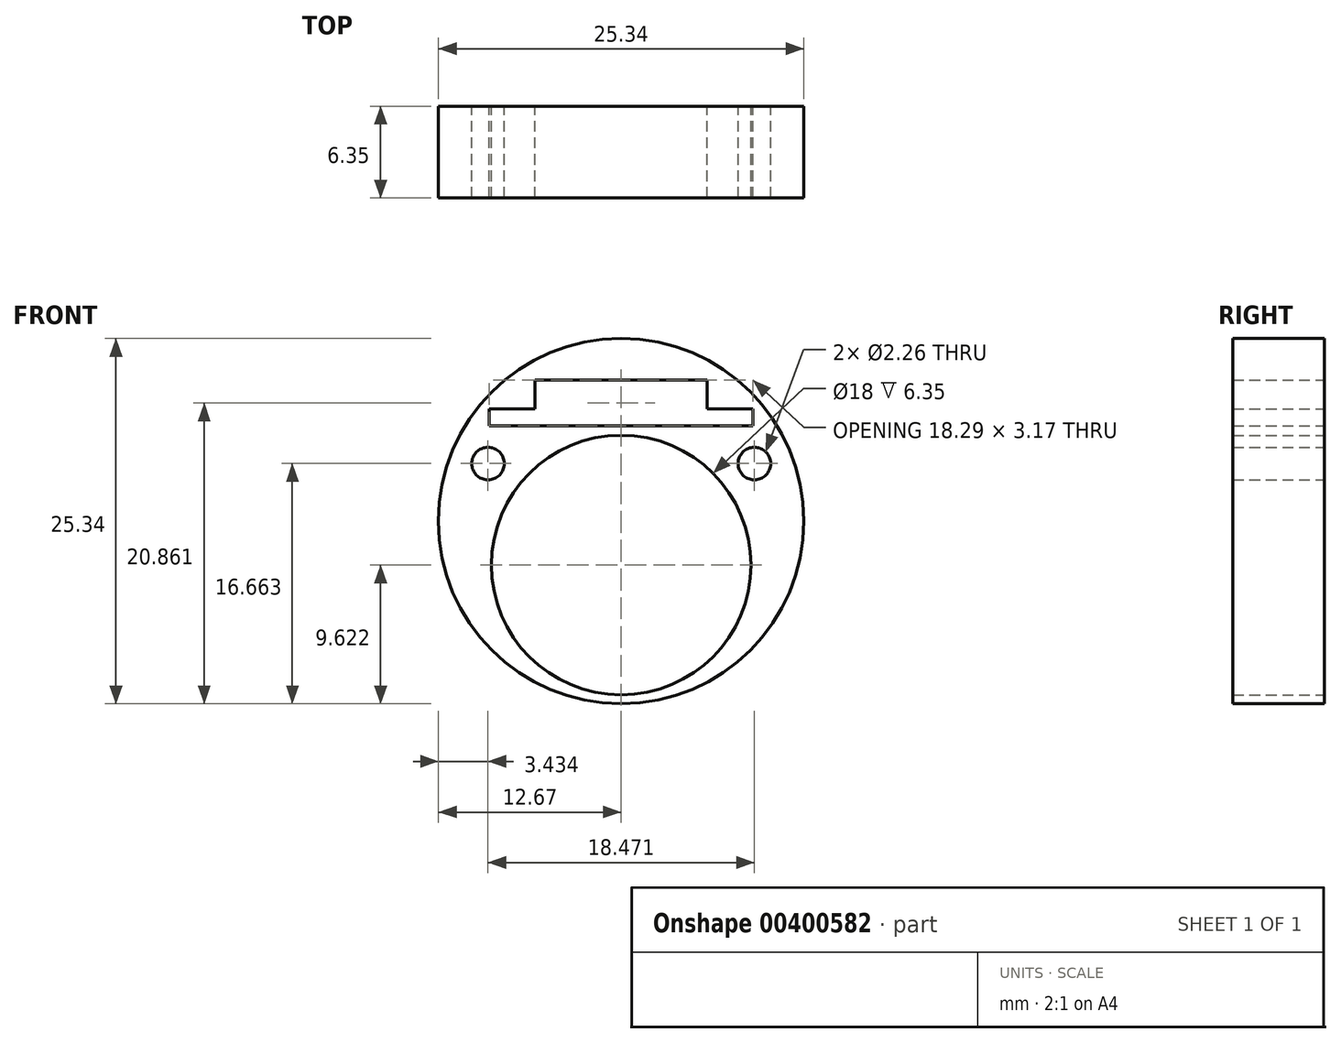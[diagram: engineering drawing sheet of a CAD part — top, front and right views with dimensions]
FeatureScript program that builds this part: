
annotation { "Feature Type Name" : "Feature", "Feature Type Description" : "" }
export const myFeature = defineFeature(function(context is Context, id is Id, definition is map)
    precondition{}
    {
        {
            var Q0;
            Q0=qCreatedBy(makeId("Front.planeOp"),FACE);
            var sketch = newSketch(context, id + "F0", { "sketchPlane" : qUnion([Q0])});
            skCircle(sketch, "E0", {"center": v(0, 0) * mm, "radius": 12.67 * mm});
            skCircle(sketch, "E1", {"center": v(0, -3.05) * mm, "radius": 9 * mm});
            skLineSegment(sketch, "E2", {"start": v(0, -3.05) * mm, "end": v(0, 0) * mm, "construction": true});
            skLineSegment(sketch, "E3.top", {"start": v(-9.14, 6.6) * mm, "end": v(9.14, 6.6) * mm});
            skLineSegment(sketch, "E3.left", {"start": v(-9.14, 7.8) * mm, "end": v(-9.14, 6.6) * mm});
            skLineSegment(sketch, "E3.right", {"start": v(9.14, 7.8) * mm, "end": v(9.14, 6.6) * mm});
            skPoint(sketch, "E4", {"position": v(0, 7.54) * mm});
            skLineSegment(sketch, "E5", {"start": v(0, 0) * mm, "end": v(0, 6.6) * mm, "construction": true});
            skLineSegment(sketch, "E6", {"start": v(-5.97, 7.8) * mm, "end": v(-5.97, 9.78) * mm});
            skLineSegment(sketch, "E7", {"start": v(-5.97, 9.78) * mm, "end": v(0, 9.78) * mm});
            skLineSegment(sketch, "E8", {"start": v(0, 9.78) * mm, "end": v(5.97, 9.78) * mm});
            skLineSegment(sketch, "E9", {"start": v(5.97, 9.78) * mm, "end": v(5.97, 7.8) * mm});
            skLineSegment(sketch, "E10", {"start": v(-9.14, 7.8) * mm, "end": v(-5.97, 7.8) * mm});
            skLineSegment(sketch, "E11", {"start": v(5.97, 7.8) * mm, "end": v(9.14, 7.8) * mm});
            skLineSegment(sketch, "E12", {"start": v(0, 0) * mm, "end": v(9.24, 4) * mm, "construction": true});
            skLineSegment(sketch, "E13", {"start": v(9.24, 4) * mm, "end": v(-9.24, 4) * mm, "construction": true});
            skLineSegment(sketch, "E14", {"start": v(-9.24, 4) * mm, "end": v(0, 0) * mm, "construction": true});
            skPoint(sketch, "E15", {"position": v(9.24, 4) * mm});
            skPoint(sketch, "E16", {"position": v(-9.24, 4) * mm});
            skCircle(sketch, "E17", {"center": v(-9.24, 4) * mm, "radius": 2.61 * mm, "construction": true});
            skSolve(sketch);
        }
        {
            var Q0;
            Q0=makeQuery(id+"F0.imprint","IMPRINT",FACE,{"disambiguationData":[TD([[makeQuery(id+"F0.imprint","IMPRINT",EDGE,{"derivedFrom":sQuery(id+"F0.wireOp",EDGE,"E0")}),1.0]])]});
            extrude(context, id + "F1", {"entities" : qUnion([Q0]), "depth" : 6.35 * mm});
        }
        {
            var Q0;
            Q0=sQuery(id+"F0.wireOp",VERTEX,"E15");
            var Q1;
            Q1=sQuery(id+"F0.wireOp",VERTEX,"E16");
            var Q2;
            Q2=makeQuery(id+"F1.opExtrude","SWEPT_BODY",BODY,{"disambiguationData":[OSD([sQuery(id+"F0.wireOp",EDGE,"E0"),sQuery(id+"F0.wireOp",EDGE,"E1"),sQuery(id+"F0.wireOp",EDGE,"E3.top"),sQuery(id+"F0.wireOp",EDGE,"E3.left"),sQuery(id+"F0.wireOp",EDGE,"E3.right"),sQuery(id+"F0.wireOp",EDGE,"E6"),sQuery(id+"F0.wireOp",EDGE,"E7"),sQuery(id+"F0.wireOp",EDGE,"E8"),sQuery(id+"F0.wireOp",EDGE,"E9"),sQuery(id+"F0.wireOp",EDGE,"E10"),sQuery(id+"F0.wireOp",EDGE,"E11")])]});
            hole(context, id + "F2", {"style" : HoleStyle.SIMPLE, "endStyle" : HoleEndStyle.THROUGH, "oppositeDirection" : true, "holeDiameter" : 2.26 * mm, "isTappedThrough" : true, "tappedDepth" : 12.7 * mm, "tapClearance" : 3, "locations" : qUnion([Q0, Q1]), "scope" : qUnion([Q2])});
        }
    });
